# Revit family: QF_ELECTROLUXPROFESSIONAL_589477_MCKDFADDPO
name_source: partatom
category: Specialty Equipment
revit_build: Autodesk Revit 2018 (Build: 20190510_1515(x64)
units: mm (PartAtom-declared; Revit-internal decimal feet)

## family parameters
Always vertical = Yes
Cut with Voids When Loaded = No
Part Type = Normal
Room Calculation Point = No
Round Connector Dimension = Use Diameter
Shared = No
Work Plane-Based = No

## types (1)
- QF_ELECTROLUXPROFESSIONAL_589477_MCKDFADDPO
    Cold Water Connection Height = 0 mm  [stored 0 ft]
    Cold Water Maximum Pressure = 0.00 psi
    Cold Water Minimum Pressure = 0.00 psi
    Cold Water Size = 1"
    Description = GAS PASTA COOKER,1X20L,1-S,400X900X800H
    Direct Waste Size = 1"
    Gas Connection Height = 0 mm  [stored 0 ft]
    Gas Input = 35794.5 Btu/h
    Gas KW = 10.5
    Gas Size = 1"
    HP = 0 HP
    Indirect Waste Connection Height = 0 mm  [stored 0 ft]
    Indirect Waste Size = 1"
    Manufacturer = ELECTROLUX
    Model = 589477
    Watts = 0 W
    Weight in Pounds = 160.9

note: [stored X ft] marks values corroborated as IEEE doubles in the binary element streams (Revit-internal decimal feet)

## geometry (parser evidence)
native form markers: Blend x12, Sweep x12
no freeform markers — native parametric forms only
